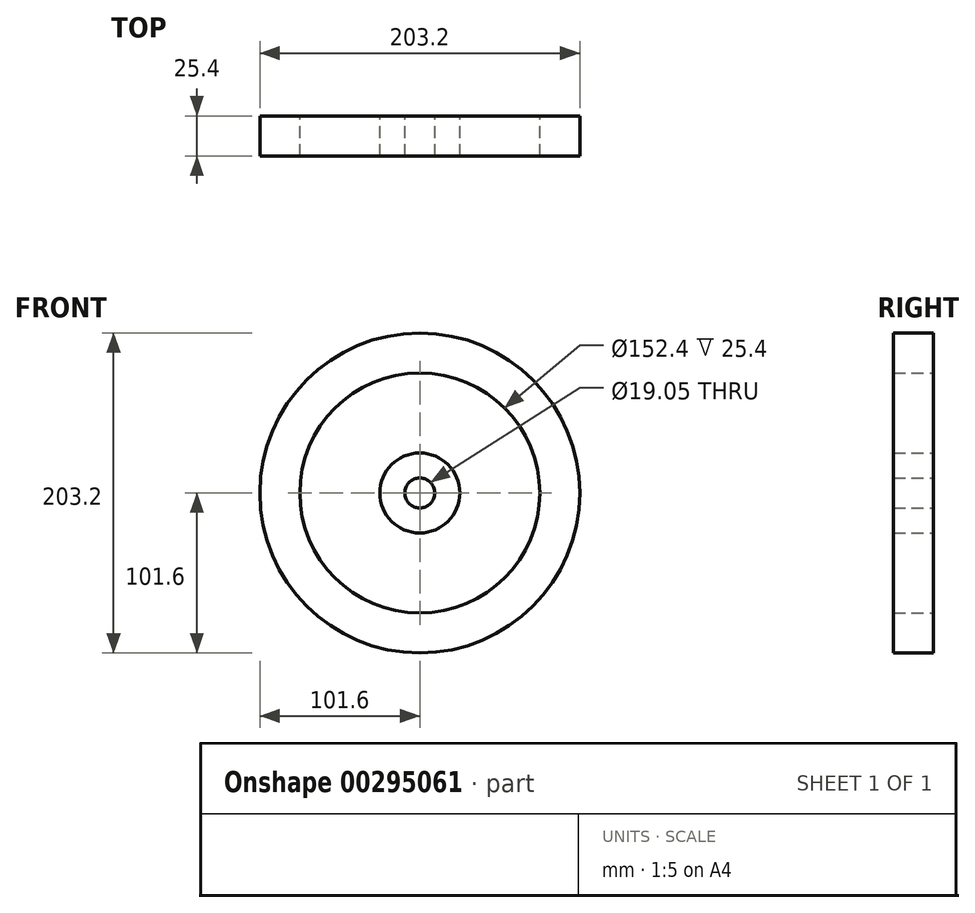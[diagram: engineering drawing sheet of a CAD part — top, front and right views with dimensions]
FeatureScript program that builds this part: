
annotation { "Feature Type Name" : "Feature", "Feature Type Description" : "" }
export const myFeature = defineFeature(function(context is Context, id is Id, definition is map)
    precondition{}
    {
        {
            var Q0;
            Q0=qCreatedBy(makeId("Front.planeOp"),FACE);
            var sketch = newSketch(context, id + "F0", { "sketchPlane" : qUnion([Q0])});
            skCircle(sketch, "E0", {"center": v(0, 0) * mm, "radius": 101.6 * mm});
            skCircle(sketch, "E1", {"center": v(0, 0) * mm, "radius": 76.2 * mm});
            skCircle(sketch, "E2", {"center": v(0, 0) * mm, "radius": 25.4 * mm});
            skCircle(sketch, "E3", {"center": v(0, 0) * mm, "radius": 9.53 * mm});
            skLineSegment(sketch, "E4.0", {"start": v(-22, 12.7) * mm, "end": v(-75.13, 12.7) * mm});
            skLineSegment(sketch, "E5.0", {"start": v(12.7, -22) * mm, "end": v(12.7, -75.13) * mm});
            skLineSegment(sketch, "E6.trimOffspring", {"start": v(22, -12.7) * mm, "end": v(75.13, -12.7) * mm});
            skLineSegment(sketch, "E7.trimOffspring", {"start": v(-12.7, -22) * mm, "end": v(-12.7, -75.13) * mm});
            skLineSegment(sketch, "E8.trimOffspring", {"start": v(-22, -12.7) * mm, "end": v(-75.13, -12.7) * mm});
            skLineSegment(sketch, "E9.0", {"start": v(12.7, 22) * mm, "end": v(12.7, 75.13) * mm});
            skLineSegment(sketch, "E10.0", {"start": v(-12.7, 22) * mm, "end": v(-12.7, 75.13) * mm});
            skPoint(sketch, "E11.trimOffspring.end.orphan", {"position": v(22.56, 12.7) * mm});
            skLineSegment(sketch, "E12", {"start": v(22.56, 12.7) * mm, "end": v(22, 12.7) * mm});
            skSolve(sketch);
        }
        {
            var Q0;
            Q0 = qSketchRegion(id + "F0", true);
            var Q1;
            Q1=makeQuery(id+"F0.imprint","IMPRINT",FACE,{"disambiguationData":[TD([[makeQuery(id+"F0.imprint","IMPRINT",EDGE,{"derivedFrom":sQuery(id+"F0.wireOp",EDGE,"E3")}),-1.0]])]});
            extrude(context, id + "F1", {"entities" : qUnion([Q0, Q1]), "depth" : 25.4 * mm});
        }
    });
